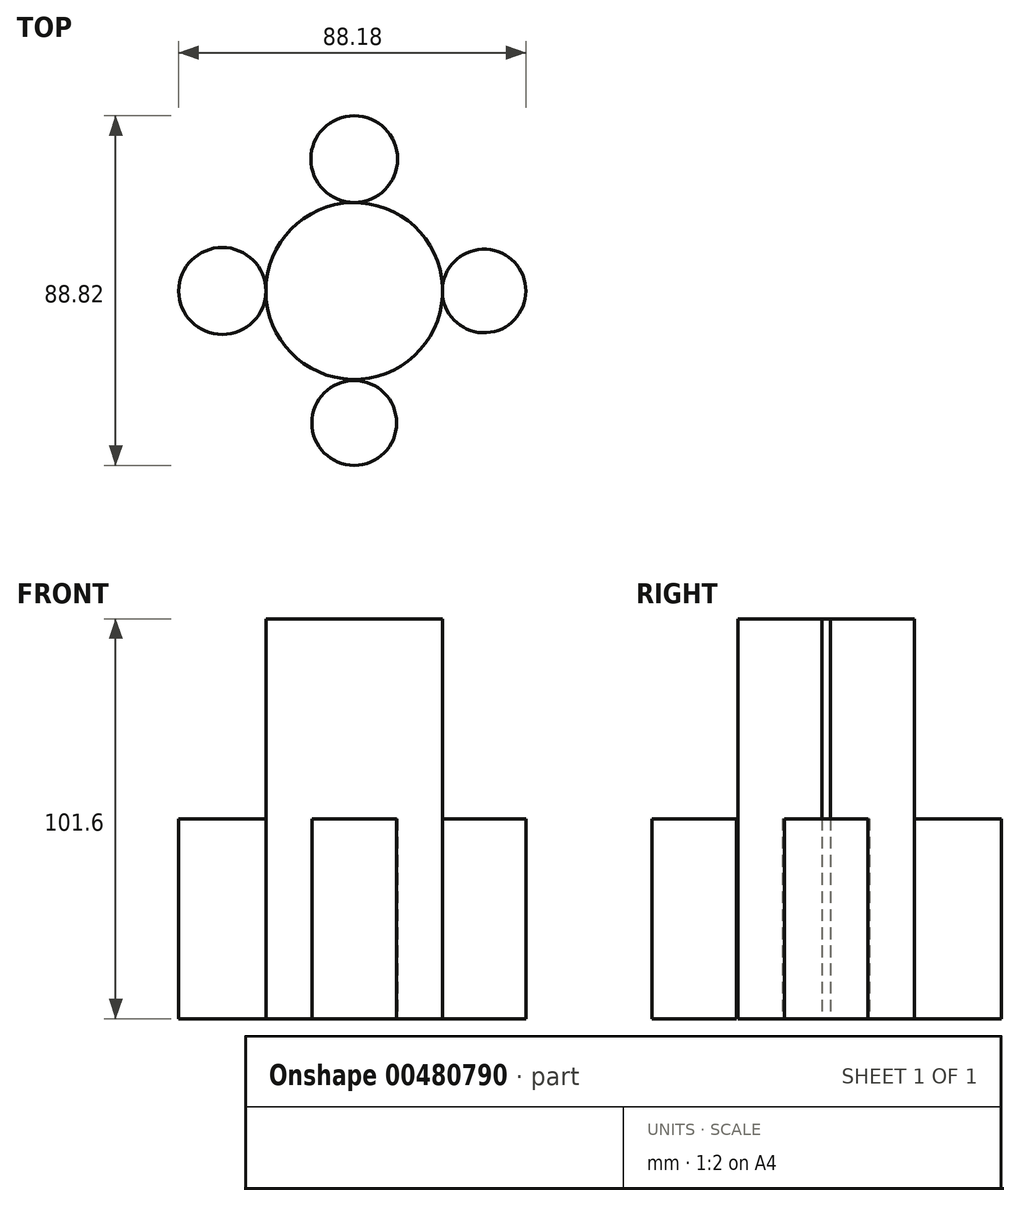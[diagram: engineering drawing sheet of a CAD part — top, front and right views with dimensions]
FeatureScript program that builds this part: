
annotation { "Feature Type Name" : "Feature", "Feature Type Description" : "" }
export const myFeature = defineFeature(function(context is Context, id is Id, definition is map)
    precondition{}
    {
        {
            var Q0;
            Q0=qCreatedBy(makeId("Top.planeOp"),FACE);
            var sketch = newSketch(context, id + "F0", { "sketchPlane" : qUnion([Q0])});
            skCircle(sketch, "E0", {"center": v(0, 0) * mm, "radius": 22.45 * mm});
            skCircle(sketch, "E1", {"center": v(32.98, 0) * mm, "radius": 10.62 * mm});
            skCircle(sketch, "E2", {"center": v(0, -33.51) * mm, "radius": 10.77 * mm});
            skCircle(sketch, "E3", {"center": v(-33.51, 0) * mm, "radius": 11.06 * mm});
            skCircle(sketch, "E4", {"center": v(0, 33.51) * mm, "radius": 11.03 * mm});
            skSolve(sketch);
        }
        {
            var Q0;
            {var subQ0=sQuery(id+"F0.wireOp",EDGE,"E0");var subQ1=makeQuery(id+"F0.imprint","INTERSECT",VERTEX,{"derivedFrom":[subQ0,sQuery(id+"F0.wireOp",EDGE,"E3")]});Q0=makeQuery(id+"F0.imprint","IMPRINT",FACE,{"disambiguationData":[TD([[makeQuery(id+"F0.imprint","IMPRINT",EDGE,{"disambiguationData":[TD([[subQ1,1.0]])],"derivedFrom":subQ0}),1.0]])]});}
            extrude(context, id + "F1", {"entities" : qUnion([Q0]), "depth" : 101.6 * mm, "offsetDistance" : 25.4 * mm});
        }
        {
            var Q0;
            Q0 = qSketchRegion(id + "F0", true);
            extrude(context, id + "F2", {"entities" : qUnion([Q0]), "operationType" : NewBodyOperationType.ADD, "depth" : 50.8 * mm, "offsetDistance" : 25.4 * mm});
        }
    });
